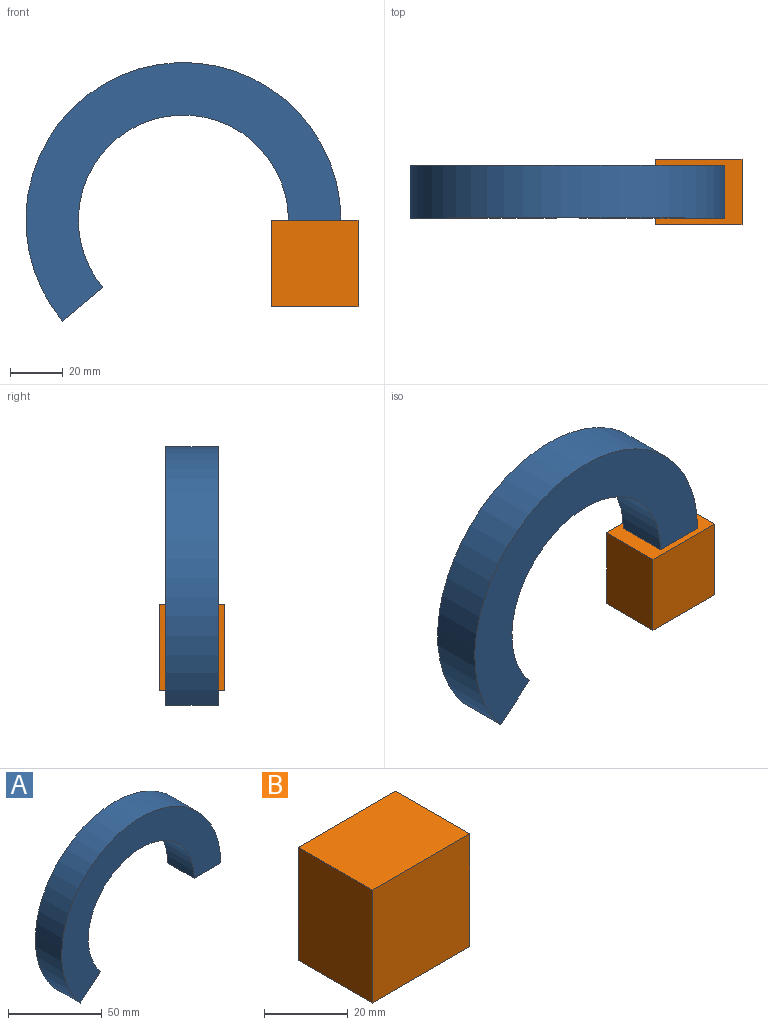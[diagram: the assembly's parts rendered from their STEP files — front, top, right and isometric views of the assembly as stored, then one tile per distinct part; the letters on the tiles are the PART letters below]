
ASSEMBLY  parts=2 mates=1
PART A: 6 faces, bbox 120x20x98.6 mm
  f0: cylinder r=60mm len=120mm, axis (0,1,0), area 4607.7mm2, adj f1,f3,f4,f5
  f1: plane 120x98.57mm, normal (0,1,0), area 3839.7mm2, adj f0,f2,f4,f5
  f2: cylinder r=40mm len=80mm, axis (0,1,0), area 3071.8mm2, adj f1,f3,f4,f5
  f3: plane 120x98.57mm, normal (0,-1,0), area 3839.7mm2, adj f0,f2,f4,f5
  f4: plane 20x15.32mm, normal (0.64,0,-0.77), area 400mm2, adj f0,f1,f2,f3
  f5: plane 20x20mm, normal (0,0,-1), area 400mm2, adj f0,f1,f2,f3
PART B: 6 faces, bbox 33x25x33 mm
  f0: plane 33x25mm, normal (1,0,0), area 825mm2, adj f1,f3,f4,f5
  f1: plane 33x25mm, normal (0,0,1), area 825mm2, adj f0,f2,f4,f5
  f2: plane 33x25mm, normal (-1,0,0), area 825mm2, adj f1,f3,f4,f5
  f3: plane 33x25mm, normal (0,0,-1), area 825mm2, adj f0,f2,f4,f5
  f4: plane 33x33mm, normal (0,-1,0), area 1089mm2, adj f0,f1,f2,f3
  f5: plane 33x33mm, normal (0,1,0), area 1089mm2, adj f0,f1,f2,f3
PLACE A at identity
PLACE B rot(axis=(0.71,0,0.71),180deg) t=(0,-12.5,-16.5)mm
MATE fastened B.f0 <-> A.f5  axis (0,0,1) through (0,0,0)mm
